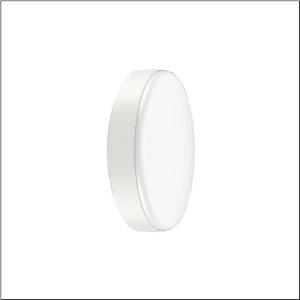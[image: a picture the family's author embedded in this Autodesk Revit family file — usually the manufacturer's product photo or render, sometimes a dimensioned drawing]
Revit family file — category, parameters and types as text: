
# Revit family: rondel_31_51wc10mb44a
name_source: partatom
category: Lighting Fixtures
units: mm (PartAtom-declared; Revit-internal decimal feet)

## family parameters
Cut with Voids When Loaded = No
Host = Face
Light Source = No
Part Type = Normal
Room Calculation Point = No
Round Connector Dimension = Use Diameter
Shared = No

## types (1)
- --- (1 x LED, 4400 lm, 34 W, 4000K)
    Apparent Load = 34 VA
    CIE Flux Codes = 44 75 94 94 100
    Color Rendering = 80
    Color Temperature = 4000K
    Default Elevation = 1800 mm
    Description = Rondel 31, wall and ceiling luminaire, primary optical cover: cover, of PC, opal, light emission: direct distribution, primary light characteristic: symmetric, installation type: surface-mounted, LED, rated luminous flux: 4.400lm, luminous efficacy: 129lm/W, light colour: 840, colour temperature: 4000K, with terminal, 3-pole, max. 2.5mm², mains connection: 220..240V, AC, 50/60Hz, rated input power: 34W, luminaire housing, of PC, traffic white (RAL 9016), diameter: 480mm, protection rating (complete): IP65, insulation class (complete): insulation class II (safety insulation), certification: CE, impact resistance: IK10, permissible operating ambient temperature: -20..+40°C, permissible storage temperature: -20..+60°C, packaging unit: 1 piece
    Height = 97 mm
    Lamp = 1 x LED
    Lamp Light Flux = 4400 lm
    Lamp Power = 34 W
    Lamp count = 1
    Length = 480 mm
    Luminous efficacy = 129 lm/W
    Manufacturer = Siteco
    ModVariant = No
    Model = 51WC10MB44A
    Mounting Place = Ceiling
    Mounting Type = Surface mounted
    Number of Poles = 1
    OnlyDefault = Yes
    Power Factor = 1
    Product Name = Rondel 31
    Product group = wall and ceiling luminaire
    ProductGroupID = 302
    Protection Class = Protection class II
    Protection Degree = IP 65
    RLX_Detail_Level = 1
    RLX_Emergency_Light_Flux = 0 lm
    RLX_Emergency_Type = 0
    RLX_Emergency_Type_DB = No
    RlxData = <blob elided: 41369 chars, md5=16aec2f8>
    Socket = socket
    Standby Power = 0 W
    System Light Flux = 4400 lm
    System Power = 34 W
    Type Comments = factory setting: luminous flux: 100 % | (ON | ON)
    Type Image = l_1007188.jpg
    URL = http://relux.com
    VarID = @adj_100993
    Voltage = 0 V
    Weight = 0.00 kg
    Width = 0 mm  [stored 0 ft]

note: [stored X ft] marks values corroborated as IEEE doubles in the binary element streams (Revit-internal decimal feet)

## geometry (parser evidence)
native form markers: Blend x4, Sweep x13
no freeform markers — native parametric forms only
